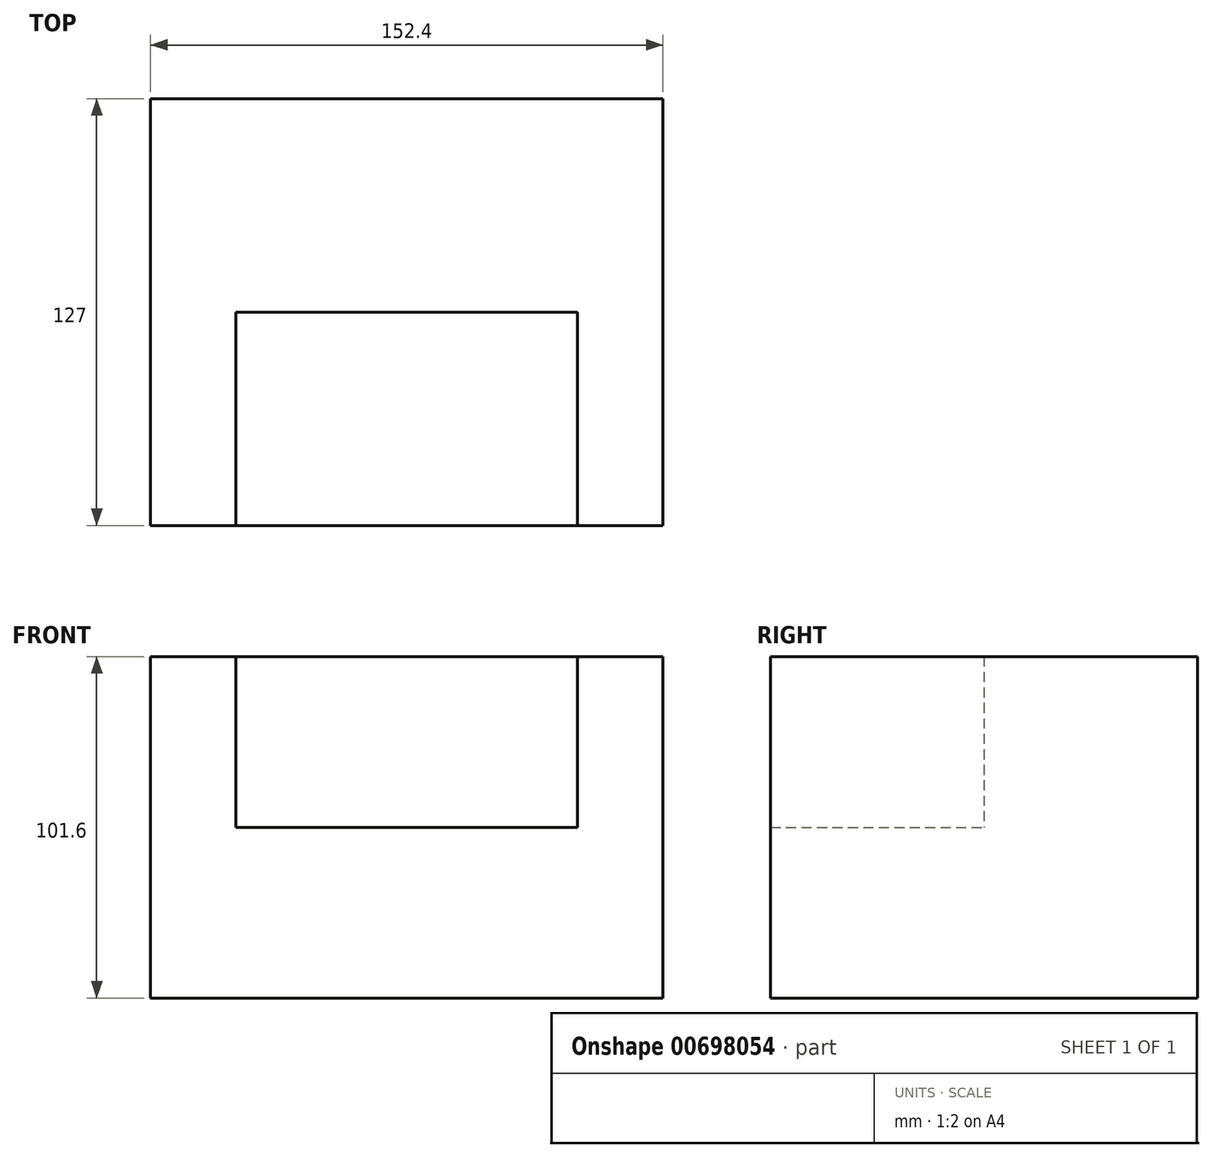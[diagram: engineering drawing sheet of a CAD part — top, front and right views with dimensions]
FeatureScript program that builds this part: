
annotation { "Feature Type Name" : "Feature", "Feature Type Description" : "" }
export const myFeature = defineFeature(function(context is Context, id is Id, definition is map)
    precondition{}
    {
        {
            var Q0;
            Q0=qCreatedBy(makeId("Front.planeOp"),FACE);
            var sketch = newSketch(context, id + "F0", { "sketchPlane" : qUnion([Q0])});
            skLineSegment(sketch, "E0", {"start": v(-25.4, -5.95) * mm, "end": v(127, -5.95) * mm});
            skLineSegment(sketch, "E1", {"start": v(127, -5.95) * mm, "end": v(127, 95.65) * mm});
            skLineSegment(sketch, "E2", {"start": v(127, 95.65) * mm, "end": v(101.6, 95.65) * mm});
            skLineSegment(sketch, "E3", {"start": v(101.6, 95.65) * mm, "end": v(101.6, 44.85) * mm});
            skLineSegment(sketch, "E4", {"start": v(101.6, 44.85) * mm, "end": v(0, 44.85) * mm});
            skLineSegment(sketch, "E5", {"start": v(0, 44.85) * mm, "end": v(0, 95.65) * mm});
            skLineSegment(sketch, "E6", {"start": v(0, 95.65) * mm, "end": v(-25.4, 95.65) * mm});
            skLineSegment(sketch, "E7", {"start": v(-25.4, 95.65) * mm, "end": v(-25.4, -5.95) * mm});
            skSolve(sketch);
        }
        {
            var Q0;
            Q0=makeQuery(id+"F0.imprint","IMPRINT",FACE,{"disambiguationData":[TD([[makeQuery(id+"F0.imprint","IMPRINT",EDGE,{"derivedFrom":sQuery(id+"F0.wireOp",EDGE,"E0")}),1.0]])]});
            extrude(context, id + "F1", {"entities" : qUnion([Q0]), "depth" : 127 * mm, "offsetDistance" : 25.4 * mm});
        }
        {
            var Q0;
            Q0=makeQuery(id+"F1.opExtrude","SWEPT_FACE",FACE,{"disambiguationData":[OSD([sQuery(id+"F0.wireOp",EDGE,"E4")])]});
            var sketch = newSketch(context, id + "F2", { "sketchPlane" : qUnion([Q0])});
            skLineSegment(sketch, "E8.bottom", {"start": v(0, 0) * mm, "end": v(101.6, 0) * mm});
            skLineSegment(sketch, "E8.top", {"start": v(0, -63.5) * mm, "end": v(101.6, -63.5) * mm});
            skLineSegment(sketch, "E8.left", {"start": v(0, 0) * mm, "end": v(0, -63.5) * mm});
            skLineSegment(sketch, "E8.right", {"start": v(101.6, 0) * mm, "end": v(101.6, -63.5) * mm});
            skSolve(sketch);
        }
        {
            var Q0;
            Q0=makeQuery(id+"F2.imprint","IMPRINT",FACE,{"disambiguationData":[TD([[makeQuery(id+"F2.imprint","IMPRINT",EDGE,{"derivedFrom":sQuery(id+"F2.wireOp",EDGE,"E8.bottom")}),1.0]])]});
            extrude(context, id + "F3", {"entities" : qUnion([Q0]), "operationType" : NewBodyOperationType.ADD, "depth" : 50.8 * mm, "offsetDistance" : 25.4 * mm});
        }
    });
